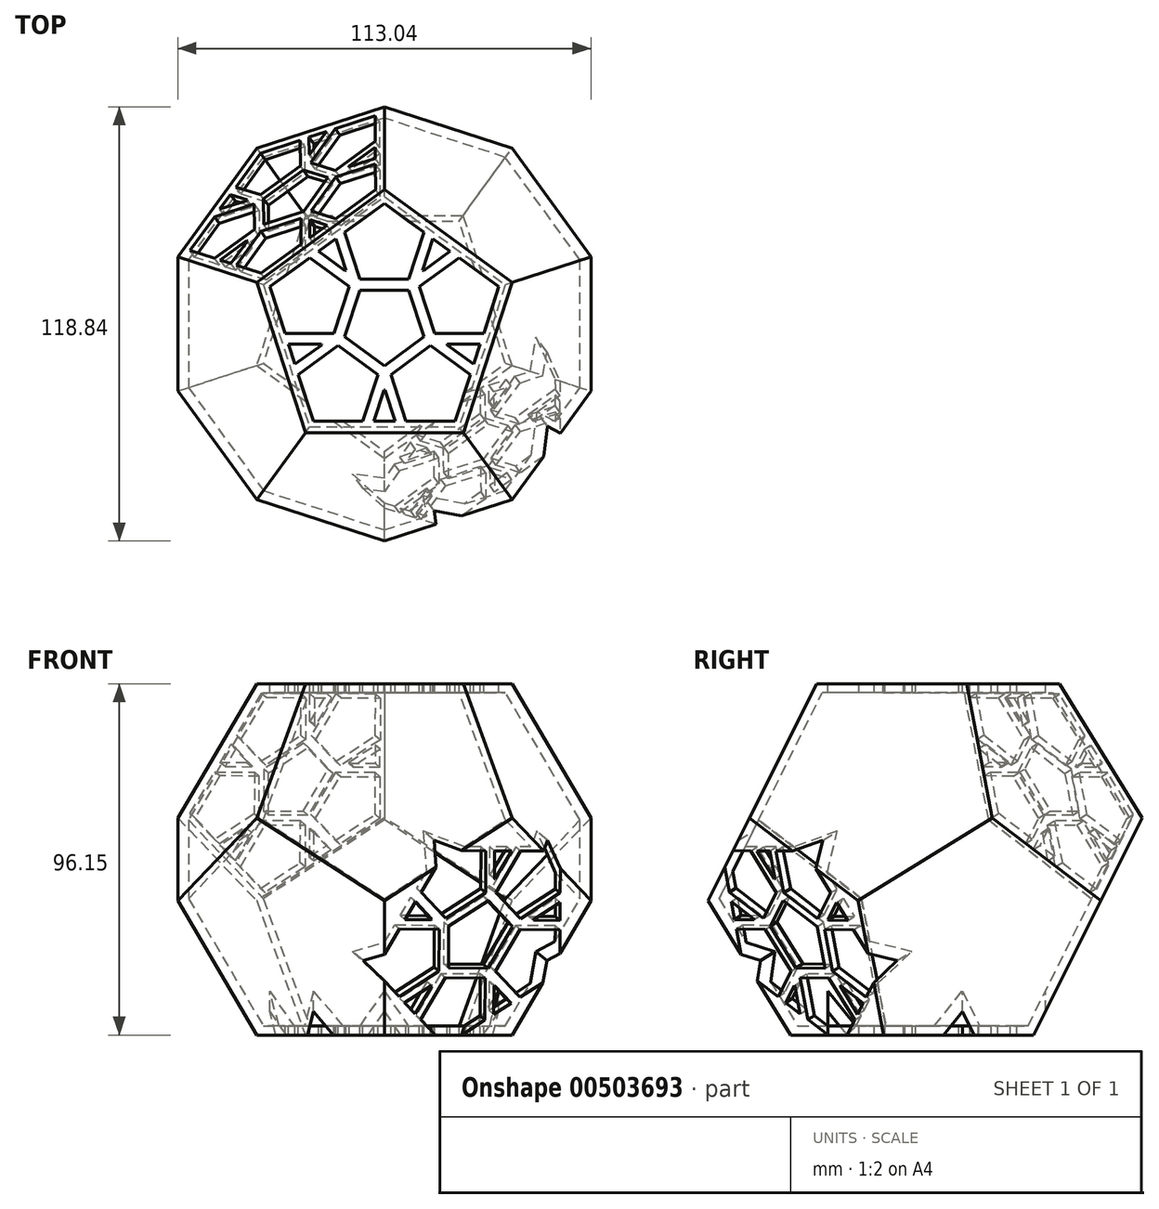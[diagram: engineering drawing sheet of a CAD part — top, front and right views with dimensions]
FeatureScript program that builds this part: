
annotation { "Feature Type Name" : "Feature", "Feature Type Description" : "" }
export const myFeature = defineFeature(function(context is Context, id is Id, definition is map)
    precondition{}
    {
        {
            var Q0;
            Q0=qCreatedBy(makeId("Top.planeOp"),FACE);
            var sketch = newSketch(context, id + "F0", { "sketchPlane" : qUnion([Q0])});
            skCircle(sketch, "E0.cCircle", {"center": v(0, 0) * mm, "radius": 29.71 * mm, "construction": true});
            skLineSegment(sketch, "E0.0", {"start": v(34.93, 11.35) * mm, "end": v(21.59, -29.71) * mm});
            skLineSegment(sketch, "E0.1", {"start": v(21.59, -29.71) * mm, "end": v(-21.59, -29.71) * mm});
            skLineSegment(sketch, "E0.2", {"start": v(-21.59, -29.71) * mm, "end": v(-34.93, 11.35) * mm});
            skLineSegment(sketch, "E0.3", {"start": v(-34.93, 11.35) * mm, "end": v(0, 36.73) * mm});
            skLineSegment(sketch, "E0.4", {"start": v(0, 36.73) * mm, "end": v(34.93, 11.35) * mm});
            skPoint(sketch, "E0.0.midPoint", {"position": v(28.26, -9.18) * mm});
            skLineSegment(sketch, "E1", {"start": v(0, 41.72) * mm, "end": v(0, -38.26) * mm, "construction": true});
            skLineSegment(sketch, "E2", {"start": v(-54.38, 0) * mm, "end": v(61.6, 0) * mm, "construction": true});
            skSolve(sketch);
        }
        {
            var Q0;
            Q0=sQuery(id+"F0.wireOp",EDGE,"E0.2");
            cPlane(context, id + "F1", {"entities" : qUnion([Q0]), "cplaneType" : CPlaneType.LINE_ANGLE, "offset" : 25 * mm, "angle" : 116.57 * degree, "width" : 150 * mm, "height" : 150 * mm});
        }
        {
            var Q0;
            Q0=qCreatedBy(id+"F1.planeOp",FACE);
            var sketch = newSketch(context, id + "F2", { "sketchPlane" : qUnion([Q0])});
            skCircle(sketch, "E3.cCircle", {"center": v(-6.18, -42.55) * mm, "radius": 29.71 * mm, "construction": true});
            skLineSegment(sketch, "E3.0", {"start": v(19.45, -16.25) * mm, "end": v(26.75, -58.8) * mm});
            skLineSegment(sketch, "E3.1", {"start": v(26.75, -58.8) * mm, "end": v(-11.46, -78.9) * mm});
            skLineSegment(sketch, "E3.2", {"start": v(-11.46, -78.9) * mm, "end": v(-42.38, -48.76) * mm});
            skLineSegment(sketch, "E3.3", {"start": v(-42.38, -48.76) * mm, "end": v(-23.27, -10.05) * mm});
            skLineSegment(sketch, "E3.4", {"start": v(-23.27, -10.05) * mm, "end": v(19.45, -16.25) * mm});
            skPoint(sketch, "E3.0.midPoint", {"position": v(23.1, -37.53) * mm});
            skSolve(sketch);
        }
        {
            var Q0;
            Q0=sQuery(id+"F0.wireOp",VERTEX,"E0.1.start");
            var Q1;
            Q1=sQuery(id+"F2.wireOp",VERTEX,"E3.4.start");
            var Q2;
            Q2=sQuery(id+"F2.wireOp",VERTEX,"E3.3.start");
            cPlane(context, id + "F3", {"entities" : qUnion([Q0, Q1, Q2]), "cplaneType" : CPlaneType.THREE_POINT, "offset" : 25 * mm, "oppositeDirection" : true, "width" : 150 * mm, "height" : 150 * mm});
        }
        {
            var Q0;
            Q0=qCreatedBy(id+"F3.planeOp",FACE);
            var sketch = newSketch(context, id + "F4", { "sketchPlane" : qUnion([Q0])});
            skCircle(sketch, "E4.cCircle", {"center": v(0, -43) * mm, "radius": 29.71 * mm, "construction": true});
            skLineSegment(sketch, "E4.0", {"start": v(21.59, -13.29) * mm, "end": v(34.93, -54.35) * mm});
            skLineSegment(sketch, "E4.1", {"start": v(34.93, -54.35) * mm, "end": v(0, -79.73) * mm});
            skLineSegment(sketch, "E4.2", {"start": v(0, -79.73) * mm, "end": v(-34.93, -54.35) * mm});
            skLineSegment(sketch, "E4.3", {"start": v(-34.93, -54.35) * mm, "end": v(-21.59, -13.29) * mm});
            skLineSegment(sketch, "E4.4", {"start": v(-21.59, -13.29) * mm, "end": v(21.59, -13.29) * mm});
            skPoint(sketch, "E4.0.midPoint", {"position": v(28.26, -33.82) * mm});
            skSolve(sketch);
        }
        {
            var Q0;
            Q0=sQuery(id+"F4.wireOp",VERTEX,"E4.2.start");
            var Q1;
            Q1=sQuery(id+"F2.wireOp",VERTEX,"E3.3.start");
            var Q2;
            Q2=sQuery(id+"F2.wireOp",VERTEX,"E3.2.start");
            cPlane(context, id + "F5", {"entities" : qUnion([Q0, Q1, Q2]), "cplaneType" : CPlaneType.THREE_POINT, "offset" : 25 * mm, "width" : 150 * mm, "height" : 150 * mm});
        }
        {
            var Q0;
            Q0=qCreatedBy(id+"F5.planeOp",FACE);
            var sketch = newSketch(context, id + "F6", { "sketchPlane" : qUnion([Q0])});
            skCircle(sketch, "E5.cCircle", {"center": v(-13.29, -40.9) * mm, "radius": 29.71 * mm, "construction": true});
            skLineSegment(sketch, "E5.0", {"start": v(-1.94, -5.97) * mm, "end": v(23.44, -40.9) * mm});
            skLineSegment(sketch, "E5.1", {"start": v(23.44, -40.9) * mm, "end": v(-1.94, -75.82) * mm});
            skLineSegment(sketch, "E5.2", {"start": v(-1.94, -75.82) * mm, "end": v(-43, -62.48) * mm});
            skLineSegment(sketch, "E5.3", {"start": v(-43, -62.48) * mm, "end": v(-43, -19.3) * mm});
            skLineSegment(sketch, "E5.4", {"start": v(-43, -19.3) * mm, "end": v(-1.94, -5.97) * mm});
            skPoint(sketch, "E5.0.midPoint", {"position": v(10.75, -23.43) * mm});
            skSolve(sketch);
        }
        {
            var Q0;
            Q0=sQuery(id+"F4.wireOp",VERTEX,"E4.3.start");
            var Q1;
            Q1=sQuery(id+"F6.wireOp",VERTEX,"E5.3.end");
            var Q2;
            Q2=sQuery(id+"F6.wireOp",VERTEX,"E5.3.start");
            cPlane(context, id + "F7", {"entities" : qUnion([Q0, Q1, Q2]), "cplaneType" : CPlaneType.THREE_POINT, "offset" : 25 * mm, "width" : 150 * mm, "height" : 150 * mm});
        }
        {
            var Q0;
            Q0=qCreatedBy(id+"F7.planeOp",FACE);
            var sketch = newSketch(context, id + "F8", { "sketchPlane" : qUnion([Q0])});
            skCircle(sketch, "E6.cCircle", {"center": v(13.29, -40.9) * mm, "radius": 29.71 * mm, "construction": true});
            skLineSegment(sketch, "E6.0", {"start": v(1.94, -5.97) * mm, "end": v(43, -19.3) * mm});
            skLineSegment(sketch, "E6.1", {"start": v(43, -19.3) * mm, "end": v(43, -62.48) * mm});
            skLineSegment(sketch, "E6.2", {"start": v(43, -62.48) * mm, "end": v(1.94, -75.82) * mm});
            skLineSegment(sketch, "E6.3", {"start": v(1.94, -75.82) * mm, "end": v(-23.44, -40.9) * mm});
            skLineSegment(sketch, "E6.4", {"start": v(-23.44, -40.9) * mm, "end": v(1.94, -5.97) * mm});
            skPoint(sketch, "E6.0.midPoint", {"position": v(22.47, -12.64) * mm});
            skSolve(sketch);
        }
        {
            var Q0;
            Q0=sQuery(id+"F4.wireOp",VERTEX,"E4.4.start");
            var Q1;
            Q1=sQuery(id+"F8.wireOp",VERTEX,"E6.0.start");
            var Q2;
            Q2=sQuery(id+"F8.wireOp",VERTEX,"E6.4.start");
            cPlane(context, id + "F9", {"entities" : qUnion([Q0, Q1, Q2]), "cplaneType" : CPlaneType.THREE_POINT, "offset" : 25 * mm, "width" : 150 * mm, "height" : 150 * mm});
        }
        {
            var Q0;
            Q0=qCreatedBy(id+"F9.planeOp",FACE);
            var sketch = newSketch(context, id + "F10", { "sketchPlane" : qUnion([Q0])});
            skCircle(sketch, "E7.cCircle", {"center": v(6.18, -42.55) * mm, "radius": 29.71 * mm, "construction": true});
            skLineSegment(sketch, "E7.0", {"start": v(-19.45, -16.25) * mm, "end": v(23.27, -10.05) * mm});
            skLineSegment(sketch, "E7.1", {"start": v(23.27, -10.05) * mm, "end": v(42.38, -48.76) * mm});
            skLineSegment(sketch, "E7.2", {"start": v(42.38, -48.76) * mm, "end": v(11.46, -78.9) * mm});
            skLineSegment(sketch, "E7.3", {"start": v(11.46, -78.9) * mm, "end": v(-26.75, -58.8) * mm});
            skLineSegment(sketch, "E7.4", {"start": v(-26.75, -58.8) * mm, "end": v(-19.45, -16.25) * mm});
            skPoint(sketch, "E7.0.midPoint", {"position": v(1.91, -13.15) * mm});
            skSolve(sketch);
        }
        {
            var Q0;
            Q0=sQuery(id+"F0.wireOp",VERTEX,"E0.4.start");
            var Q1;
            Q1=sQuery(id+"F10.wireOp",VERTEX,"E7.0.start");
            var Q2;
            Q2=sQuery(id+"F10.wireOp",VERTEX,"E7.4.start");
            cPlane(context, id + "F11", {"entities" : qUnion([Q0, Q1, Q2]), "cplaneType" : CPlaneType.THREE_POINT, "offset" : 25 * mm, "width" : 150 * mm, "height" : 150 * mm});
        }
        {
            var Q0;
            Q0=qCreatedBy(id+"F11.planeOp",FACE);
            var sketch = newSketch(context, id + "F12", { "sketchPlane" : qUnion([Q0])});
            skCircle(sketch, "E8.cCircle", {"center": v(13.29, -40.9) * mm, "radius": 29.71 * mm, "construction": true});
            skLineSegment(sketch, "E8.0", {"start": v(-16.42, -19.3) * mm, "end": v(24.64, -5.97) * mm});
            skLineSegment(sketch, "E8.1", {"start": v(24.64, -5.97) * mm, "end": v(50.01, -40.9) * mm});
            skLineSegment(sketch, "E8.2", {"start": v(50.01, -40.9) * mm, "end": v(24.64, -75.82) * mm});
            skLineSegment(sketch, "E8.3", {"start": v(24.64, -75.82) * mm, "end": v(-16.42, -62.48) * mm});
            skLineSegment(sketch, "E8.4", {"start": v(-16.42, -62.48) * mm, "end": v(-16.42, -19.3) * mm});
            skPoint(sketch, "E8.0.midPoint", {"position": v(4.1, -12.64) * mm});
            skSolve(sketch);
        }
        {
            var Q0;
            Q0=sQuery(id+"F2.wireOp",VERTEX,"E3.0.start");
            var Q1;
            Q1=sQuery(id+"F12.wireOp",VERTEX,"E8.0.start");
            var Q2;
            Q2=sQuery(id+"F12.wireOp",VERTEX,"E8.4.start");
            cPlane(context, id + "F13", {"entities" : qUnion([Q0, Q1, Q2]), "cplaneType" : CPlaneType.THREE_POINT, "offset" : 25 * mm, "width" : 150 * mm, "height" : 150 * mm});
        }
        {
            var Q0;
            Q0=qCreatedBy(id+"F13.planeOp",FACE);
            var sketch = newSketch(context, id + "F14", { "sketchPlane" : qUnion([Q0])});
            skCircle(sketch, "E9.cCircle", {"center": v(-13.29, -40.9) * mm, "radius": 29.71 * mm, "construction": true});
            skLineSegment(sketch, "E9.0", {"start": v(-50.01, -40.9) * mm, "end": v(-24.64, -5.97) * mm});
            skLineSegment(sketch, "E9.1", {"start": v(-24.64, -5.97) * mm, "end": v(16.42, -19.3) * mm});
            skLineSegment(sketch, "E9.2", {"start": v(16.42, -19.3) * mm, "end": v(16.42, -62.48) * mm});
            skLineSegment(sketch, "E9.3", {"start": v(16.42, -62.48) * mm, "end": v(-24.64, -75.82) * mm});
            skLineSegment(sketch, "E9.4", {"start": v(-24.64, -75.82) * mm, "end": v(-50.01, -40.9) * mm});
            skPoint(sketch, "E9.0.midPoint", {"position": v(-37.33, -23.43) * mm});
            skSolve(sketch);
        }
        {
            var Q0;
            Q0=sQuery(id+"F6.wireOp",VERTEX,"E5.1.start");
            var Q1;
            Q1=sQuery(id+"F14.wireOp",VERTEX,"E9.0.start");
            var Q2;
            Q2=sQuery(id+"F14.wireOp",VERTEX,"E9.4.start");
            cPlane(context, id + "F15", {"entities" : qUnion([Q0, Q1, Q2]), "cplaneType" : CPlaneType.THREE_POINT, "offset" : 25 * mm, "width" : 150 * mm, "height" : 150 * mm});
        }
        {
            var Q0;
            Q0=qCreatedBy(id+"F15.planeOp",FACE);
            var sketch = newSketch(context, id + "F16", { "sketchPlane" : qUnion([Q0])});
            skCircle(sketch, "E10.cCircle", {"center": v(-6.18, -42.55) * mm, "radius": 29.71 * mm, "construction": true});
            skLineSegment(sketch, "E10.0", {"start": v(-39.12, -26.3) * mm, "end": v(-0.9, -6.2) * mm});
            skLineSegment(sketch, "E10.1", {"start": v(-0.9, -6.2) * mm, "end": v(30.01, -36.34) * mm});
            skLineSegment(sketch, "E10.2", {"start": v(30.01, -36.34) * mm, "end": v(10.9, -75.06) * mm});
            skLineSegment(sketch, "E10.3", {"start": v(10.9, -75.06) * mm, "end": v(-31.82, -68.85) * mm});
            skLineSegment(sketch, "E10.4", {"start": v(-31.82, -68.85) * mm, "end": v(-39.12, -26.3) * mm});
            skPoint(sketch, "E10.0.midPoint", {"position": v(-20, -16.25) * mm});
            skSolve(sketch);
        }
        {
            var Q0;
            Q0=sQuery(id+"F12.wireOp",VERTEX,"E8.1.end");
            var Q1;
            Q1=sQuery(id+"F10.wireOp",VERTEX,"E7.3.start");
            var Q2;
            Q2=sQuery(id+"F8.wireOp",VERTEX,"E6.3.start");
            cPlane(context, id + "F17", {"entities" : qUnion([Q0, Q1, Q2]), "cplaneType" : CPlaneType.THREE_POINT, "offset" : 25 * mm, "width" : 150 * mm, "height" : 150 * mm});
        }
        {
            var Q0;
            Q0=qCreatedBy(id+"F17.planeOp",FACE);
            var sketch = newSketch(context, id + "F18", { "sketchPlane" : qUnion([Q0])});
            skCircle(sketch, "E11.cCircle", {"center": v(6.18, -42.55) * mm, "radius": 29.71 * mm, "construction": true});
            skLineSegment(sketch, "E11.0", {"start": v(-30.01, -36.34) * mm, "end": v(0.9, -6.2) * mm});
            skLineSegment(sketch, "E11.1", {"start": v(0.9, -6.2) * mm, "end": v(39.12, -26.3) * mm});
            skLineSegment(sketch, "E11.2", {"start": v(39.12, -26.3) * mm, "end": v(31.82, -68.85) * mm});
            skLineSegment(sketch, "E11.3", {"start": v(31.82, -68.85) * mm, "end": v(-10.9, -75.06) * mm});
            skLineSegment(sketch, "E11.4", {"start": v(-10.9, -75.06) * mm, "end": v(-30.01, -36.34) * mm});
            skPoint(sketch, "E11.0.midPoint", {"position": v(-14.56, -21.28) * mm});
            skSolve(sketch);
        }
        {
            var Q0;
            Q0=sQuery(id+"F18.wireOp",VERTEX,"E11.4.start");
            var Q1;
            Q1=sQuery(id+"F18.wireOp",VERTEX,"E11.3.start");
            var Q2;
            Q2=sQuery(id+"F8.wireOp",VERTEX,"E6.2.start");
            cPlane(context, id + "F19", {"entities" : qUnion([Q0, Q1, Q2]), "cplaneType" : CPlaneType.THREE_POINT, "offset" : 25 * mm, "width" : 150 * mm, "height" : 150 * mm});
        }
        {
            var Q0;
            Q0=qCreatedBy(id+"F19.planeOp",FACE);
            var sketch = newSketch(context, id + "F20", { "sketchPlane" : qUnion([Q0])});
            skCircle(sketch, "E12.cCircle", {"center": v(0, 0) * mm, "radius": 29.71 * mm, "construction": true});
            skLineSegment(sketch, "E12.0", {"start": v(-34.93, -11.35) * mm, "end": v(-21.59, 29.71) * mm});
            skLineSegment(sketch, "E12.1", {"start": v(-21.59, 29.71) * mm, "end": v(21.59, 29.71) * mm});
            skLineSegment(sketch, "E12.2", {"start": v(21.59, 29.71) * mm, "end": v(34.93, -11.35) * mm});
            skLineSegment(sketch, "E12.3", {"start": v(34.93, -11.35) * mm, "end": v(0, -36.73) * mm});
            skLineSegment(sketch, "E12.4", {"start": v(0, -36.73) * mm, "end": v(-34.93, -11.35) * mm});
            skPoint(sketch, "E12.0.midPoint", {"position": v(-28.26, 9.18) * mm});
            skSolve(sketch);
        }
        {
            var Q0;
            Q0=sQuery(id+"F20.wireOp",VERTEX,"E12.2.start");
            var Q1;
            Q1=sQuery(id+"F20.wireOp",VERTEX,"E12.1.start");
            var Q2;
            Q2=sQuery(id+"F14.wireOp",VERTEX,"E9.4.start");
            cPlane(context, id + "F21", {"entities" : qUnion([Q0, Q1, Q2]), "cplaneType" : CPlaneType.THREE_POINT, "offset" : 25 * mm, "width" : 150 * mm, "height" : 150 * mm});
        }
        {
            var Q0;
            Q0=qCreatedBy(id+"F21.planeOp",FACE);
            var sketch = newSketch(context, id + "F22", { "sketchPlane" : qUnion([Q0])});
            skCircle(sketch, "E13.cCircle", {"center": v(0, -43) * mm, "radius": 29.71 * mm, "construction": true});
            skLineSegment(sketch, "E13.0", {"start": v(-34.93, -31.65) * mm, "end": v(0, -6.27) * mm});
            skLineSegment(sketch, "E13.1", {"start": v(0, -6.27) * mm, "end": v(34.93, -31.65) * mm});
            skLineSegment(sketch, "E13.2", {"start": v(34.93, -31.65) * mm, "end": v(21.59, -72.71) * mm});
            skLineSegment(sketch, "E13.3", {"start": v(21.59, -72.71) * mm, "end": v(-21.59, -72.71) * mm});
            skLineSegment(sketch, "E13.4", {"start": v(-21.59, -72.71) * mm, "end": v(-34.93, -31.65) * mm});
            skPoint(sketch, "E13.0.midPoint", {"position": v(-17.46, -18.96) * mm});
            skSolve(sketch);
        }
        {
            var Q0;
            Q0=makeQuery(id+"F2.imprint","IMPRINT",FACE,{"disambiguationData":[TD([[makeQuery(id+"F2.imprint","IMPRINT",EDGE,{"derivedFrom":sQuery(id+"F2.wireOp",EDGE,"E3.0")}),-1.0]])]});
            extrude(context, id + "F23", {"entities" : qUnion([Q0]), "depth" : 2.5 * mm});
        }
        {
            var Q0;
            Q0=makeQuery(id+"F4.imprint","IMPRINT",FACE,{"disambiguationData":[TD([[makeQuery(id+"F4.imprint","IMPRINT",EDGE,{"derivedFrom":sQuery(id+"F4.wireOp",EDGE,"E4.0")}),-1.0]])]});
            extrude(context, id + "F24", {"entities" : qUnion([Q0]), "operationType" : NewBodyOperationType.ADD, "depth" : 2.5 * mm});
        }
        {
            var Q0;
            Q0=makeQuery(id+"F0.imprint","IMPRINT",FACE,{"disambiguationData":[TD([[makeQuery(id+"F0.imprint","IMPRINT",EDGE,{"derivedFrom":sQuery(id+"F0.wireOp",EDGE,"E0.0")}),-1.0]])]});
            extrude(context, id + "F25", {"entities" : qUnion([Q0]), "operationType" : NewBodyOperationType.ADD, "oppositeDirection" : true, "depth" : 2.5 * mm});
        }
        {
            var Q0;
            Q0=makeQuery(id+"F10.imprint","IMPRINT",FACE,{"disambiguationData":[TD([[makeQuery(id+"F10.imprint","IMPRINT",EDGE,{"derivedFrom":sQuery(id+"F10.wireOp",EDGE,"E7.0")}),-1.0]])]});
            extrude(context, id + "F26", {"entities" : qUnion([Q0]), "operationType" : NewBodyOperationType.ADD, "depth" : 2.5 * mm});
        }
        {
            var Q0;
            Q0=makeQuery(id+"F8.imprint","IMPRINT",FACE,{"disambiguationData":[TD([[makeQuery(id+"F8.imprint","IMPRINT",EDGE,{"derivedFrom":sQuery(id+"F8.wireOp",EDGE,"E6.0")}),-1.0]])]});
            extrude(context, id + "F27", {"entities" : qUnion([Q0]), "operationType" : NewBodyOperationType.ADD, "depth" : 2.5 * mm});
        }
        {
            var Q0;
            Q0=makeQuery(id+"F6.imprint","IMPRINT",FACE,{"disambiguationData":[TD([[makeQuery(id+"F6.imprint","IMPRINT",EDGE,{"derivedFrom":sQuery(id+"F6.wireOp",EDGE,"E5.0")}),-1.0]])]});
            extrude(context, id + "F28", {"entities" : qUnion([Q0]), "operationType" : NewBodyOperationType.ADD, "depth" : 2.5 * mm});
        }
        {
            var Q0;
            Q0=makeQuery(id+"F16.imprint","IMPRINT",FACE,{"disambiguationData":[TD([[makeQuery(id+"F16.imprint","IMPRINT",EDGE,{"derivedFrom":sQuery(id+"F16.wireOp",EDGE,"E10.0")}),-1.0]])]});
            extrude(context, id + "F29", {"entities" : qUnion([Q0]), "operationType" : NewBodyOperationType.ADD, "depth" : 2.5 * mm});
        }
        {
            var Q0;
            Q0=makeQuery(id+"F14.imprint","IMPRINT",FACE,{"disambiguationData":[TD([[makeQuery(id+"F14.imprint","IMPRINT",EDGE,{"derivedFrom":sQuery(id+"F14.wireOp",EDGE,"E9.0")}),-1.0]])]});
            extrude(context, id + "F30", {"entities" : qUnion([Q0]), "operationType" : NewBodyOperationType.ADD, "depth" : 2.5 * mm});
        }
        {
            var Q0;
            Q0=makeQuery(id+"F12.imprint","IMPRINT",FACE,{"disambiguationData":[TD([[makeQuery(id+"F12.imprint","IMPRINT",EDGE,{"derivedFrom":sQuery(id+"F12.wireOp",EDGE,"E8.0")}),-1.0]])]});
            extrude(context, id + "F31", {"entities" : qUnion([Q0]), "operationType" : NewBodyOperationType.ADD, "depth" : 2.5 * mm});
        }
        {
            var Q0;
            Q0=makeQuery(id+"F18.imprint","IMPRINT",FACE,{"disambiguationData":[TD([[makeQuery(id+"F18.imprint","IMPRINT",EDGE,{"derivedFrom":sQuery(id+"F18.wireOp",EDGE,"E11.0")}),-1.0]])]});
            extrude(context, id + "F32", {"entities" : qUnion([Q0]), "operationType" : NewBodyOperationType.ADD, "depth" : 2.5 * mm});
        }
        {
            var Q0;
            Q0=makeQuery(id+"F20.imprint","IMPRINT",FACE,{"disambiguationData":[TD([[makeQuery(id+"F20.imprint","IMPRINT",EDGE,{"derivedFrom":sQuery(id+"F20.wireOp",EDGE,"E12.0")}),-1.0]])]});
            extrude(context, id + "F33", {"entities" : qUnion([Q0]), "operationType" : NewBodyOperationType.ADD, "depth" : 2.5 * mm});
        }
        {
            var Q0;
            Q0=makeQuery(id+"F22.imprint","IMPRINT",FACE,{"disambiguationData":[TD([[makeQuery(id+"F22.imprint","IMPRINT",EDGE,{"derivedFrom":sQuery(id+"F22.wireOp",EDGE,"E13.0")}),-1.0]])]});
            extrude(context, id + "F34", {"entities" : qUnion([Q0]), "operationType" : NewBodyOperationType.ADD, "depth" : 2.5 * mm});
        }
        {
            var Q0;
            Q0=makeQuery(id+"F25.opExtrude","CAP_FACE",FACE,{"disambiguationData":[OSD([sQuery(id+"F0.wireOp",EDGE,"E0.0"),sQuery(id+"F0.wireOp",EDGE,"E0.1"),sQuery(id+"F0.wireOp",EDGE,"E0.2"),sQuery(id+"F0.wireOp",EDGE,"E0.3"),sQuery(id+"F0.wireOp",EDGE,"E0.4")])],"isStart":true});
            var sketch = newSketch(context, id + "F35", { "sketchPlane" : qUnion([Q0])});
            skLineSegment(sketch, "E14", {"start": v(-34.93, 11.35) * mm, "end": v(0, 36.73) * mm});
            skLineSegment(sketch, "E15", {"start": v(0, 36.73) * mm, "end": v(34.93, 11.35) * mm});
            skLineSegment(sketch, "E16", {"start": v(34.93, 11.35) * mm, "end": v(21.59, -29.71) * mm});
            skLineSegment(sketch, "E17", {"start": v(21.59, -29.71) * mm, "end": v(-21.59, -29.71) * mm});
            skLineSegment(sketch, "E18", {"start": v(-21.59, -29.71) * mm, "end": v(-34.93, 11.35) * mm});
            skCircle(sketch, "E19.cCircle", {"center": v(-12.64, -17.4) * mm, "radius": 9.25 * mm, "construction": true});
            skLineSegment(sketch, "E19.0", {"start": v(-12.64, -5.96) * mm, "end": v(-1.76, -13.86) * mm});
            skLineSegment(sketch, "E19.1", {"start": v(-1.76, -13.86) * mm, "end": v(-5.92, -26.64) * mm});
            skLineSegment(sketch, "E19.2", {"start": v(-5.92, -26.64) * mm, "end": v(-19.36, -26.64) * mm});
            skLineSegment(sketch, "E19.3", {"start": v(-19.36, -26.64) * mm, "end": v(-23.51, -13.86) * mm});
            skLineSegment(sketch, "E19.4", {"start": v(-23.51, -13.86) * mm, "end": v(-12.64, -5.96) * mm});
            skPoint(sketch, "E19.0.midPoint", {"position": v(-7.2, -9.91) * mm});
            skCircle(sketch, "E20.cCircle", {"center": v(0, 21.5) * mm, "radius": 9.25 * mm, "construction": true});
            skLineSegment(sketch, "E20.0", {"start": v(6.72, 12.25) * mm, "end": v(-6.72, 12.25) * mm});
            skLineSegment(sketch, "E20.1", {"start": v(-6.72, 12.25) * mm, "end": v(-10.87, 25.03) * mm});
            skLineSegment(sketch, "E20.2", {"start": v(-10.87, 25.03) * mm, "end": v(0, 32.93) * mm});
            skLineSegment(sketch, "E20.3", {"start": v(0, 32.93) * mm, "end": v(10.87, 25.03) * mm});
            skLineSegment(sketch, "E20.4", {"start": v(10.87, 25.03) * mm, "end": v(6.72, 12.25) * mm});
            skPoint(sketch, "E20.0.midPoint", {"position": v(0, 12.25) * mm});
            skCircle(sketch, "E21.cCircle", {"center": v(0, 0) * mm, "radius": 9.25 * mm, "construction": true});
            skLineSegment(sketch, "E21.0", {"start": v(-6.72, 9.25) * mm, "end": v(6.72, 9.25) * mm});
            skLineSegment(sketch, "E21.1", {"start": v(6.72, 9.25) * mm, "end": v(10.87, -3.53) * mm});
            skLineSegment(sketch, "E21.2", {"start": v(10.87, -3.53) * mm, "end": v(0, -11.43) * mm});
            skLineSegment(sketch, "E21.3", {"start": v(0, -11.43) * mm, "end": v(-10.87, -3.53) * mm});
            skLineSegment(sketch, "E21.4", {"start": v(-10.87, -3.53) * mm, "end": v(-6.72, 9.25) * mm});
            skPoint(sketch, "E21.0.midPoint", {"position": v(0, 9.25) * mm});
            skPoint(sketch, "E22", {"position": v(28.26, -9.18) * mm});
            skPoint(sketch, "E23", {"position": v(17.46, 24.04) * mm});
            skPoint(sketch, "E24", {"position": v(-17.46, 24.04) * mm});
            skPoint(sketch, "E25", {"position": v(-28.26, -9.18) * mm});
            skPoint(sketch, "E26", {"position": v(0, -29.71) * mm});
            skLineSegment(sketch, "E27", {"start": v(17.46, 24.04) * mm, "end": v(-21.59, -29.71) * mm, "construction": true});
            skLineSegment(sketch, "E28", {"start": v(-17.46, 24.04) * mm, "end": v(21.59, -29.71) * mm});
            skLineSegment(sketch, "E29", {"start": v(28.26, -9.18) * mm, "end": v(-34.93, 11.35) * mm, "construction": true});
            skLineSegment(sketch, "E30", {"start": v(-28.26, -9.18) * mm, "end": v(34.93, 11.35) * mm, "construction": true});
            skCircle(sketch, "E31.cCircle", {"center": v(-20.45, 6.64) * mm, "radius": 9.25 * mm, "construction": true});
            skLineSegment(sketch, "E31.0", {"start": v(-9.57, 10.18) * mm, "end": v(-13.73, -2.6) * mm});
            skLineSegment(sketch, "E31.1", {"start": v(-13.73, -2.6) * mm, "end": v(-27.17, -2.6) * mm});
            skLineSegment(sketch, "E31.2", {"start": v(-27.17, -2.6) * mm, "end": v(-31.32, 10.18) * mm});
            skLineSegment(sketch, "E31.3", {"start": v(-31.32, 10.18) * mm, "end": v(-20.45, 18.08) * mm});
            skLineSegment(sketch, "E31.4", {"start": v(-20.45, 18.08) * mm, "end": v(-9.57, 10.18) * mm});
            skPoint(sketch, "E31.0.midPoint", {"position": v(-11.65, 3.79) * mm});
            skCircle(sketch, "E32.cCircle", {"center": v(20.45, 6.64) * mm, "radius": 9.25 * mm, "construction": true});
            skLineSegment(sketch, "E32.0", {"start": v(9.57, 10.18) * mm, "end": v(13.73, -2.6) * mm});
            skLineSegment(sketch, "E32.1", {"start": v(20.45, 18.08) * mm, "end": v(9.57, 10.18) * mm});
            skLineSegment(sketch, "E32.2", {"start": v(31.32, 10.18) * mm, "end": v(20.45, 18.08) * mm});
            skLineSegment(sketch, "E32.3", {"start": v(27.17, -2.6) * mm, "end": v(31.32, 10.18) * mm});
            skLineSegment(sketch, "E32.4", {"start": v(13.73, -2.6) * mm, "end": v(27.17, -2.6) * mm});
            skPoint(sketch, "E32.0.midPoint", {"position": v(11.65, 3.79) * mm});
            skLineSegment(sketch, "E33", {"start": v(0, 36.73) * mm, "end": v(0, -29.71) * mm, "construction": true});
            skLineSegment(sketch, "E34", {"start": v(-9.57, 10.18) * mm, "end": v(-6.72, 12.25) * mm, "construction": true});
            skLineSegment(sketch, "E35", {"start": v(6.72, 12.25) * mm, "end": v(9.57, 10.18) * mm, "construction": true});
            skLineSegment(sketch, "E36", {"start": v(-12.64, -5.96) * mm, "end": v(-13.73, -2.6) * mm, "construction": true});
            skCircle(sketch, "E37.cCircle", {"center": v(12.64, -17.4) * mm, "radius": 9.25 * mm, "construction": true});
            skLineSegment(sketch, "E37.0", {"start": v(23.51, -13.86) * mm, "end": v(19.36, -26.64) * mm});
            skLineSegment(sketch, "E37.1", {"start": v(19.36, -26.64) * mm, "end": v(5.92, -26.64) * mm});
            skLineSegment(sketch, "E37.2", {"start": v(5.92, -26.64) * mm, "end": v(1.76, -13.86) * mm});
            skLineSegment(sketch, "E37.3", {"start": v(1.76, -13.86) * mm, "end": v(12.64, -5.96) * mm});
            skLineSegment(sketch, "E37.4", {"start": v(12.64, -5.96) * mm, "end": v(23.51, -13.86) * mm});
            skPoint(sketch, "E37.0.midPoint", {"position": v(21.43, -20.25) * mm});
            skPoint(sketch, "E38", {"position": v(7.2, -9.91) * mm});
            skLineSegment(sketch, "E39", {"start": v(12.64, -5.96) * mm, "end": v(13.73, -2.6) * mm, "construction": true});
            skLineSegment(sketch, "E40", {"start": v(-1.76, -13.86) * mm, "end": v(1.76, -13.86) * mm, "construction": true});
            skPoint(sketch, "E41", {"position": v(-8.8, 2.86) * mm});
            skPoint(sketch, "E42", {"position": v(8.8, 2.86) * mm});
            skPoint(sketch, "E43", {"position": v(33.97, 29.48) * mm});
            skPoint(sketch, "E44", {"position": v(-5.44, -7.48) * mm});
            skPoint(sketch, "E45", {"position": v(5.44, -7.48) * mm});
            skLineSegment(sketch, "E46", {"start": v(0, 12.25) * mm, "end": v(0, 9.25) * mm, "construction": true});
            skLineSegment(sketch, "E47", {"start": v(-11.65, 3.79) * mm, "end": v(-8.8, 2.86) * mm, "construction": true});
            skLineSegment(sketch, "E48", {"start": v(11.65, 3.79) * mm, "end": v(8.8, 2.86) * mm, "construction": true});
            skLineSegment(sketch, "E49", {"start": v(5.44, -7.48) * mm, "end": v(7.2, -9.91) * mm, "construction": true});
            skLineSegment(sketch, "E50", {"start": v(-5.44, -7.48) * mm, "end": v(-7.2, -9.91) * mm, "construction": true});
            skLineSegment(sketch, "E51", {"start": v(-18.02, 19.84) * mm, "end": v(-13.3, 23.27) * mm});
            skPoint(sketch, "E52", {"position": v(-15.66, 21.56) * mm});
            skLineSegment(sketch, "E53", {"start": v(-20.45, 18.08) * mm, "end": v(-10.87, 25.03) * mm, "construction": true});
            skLineSegment(sketch, "E54", {"start": v(-10.74, 14.55) * mm, "end": v(-10.52, 14.71) * mm});
            skLineSegment(sketch, "E55", {"start": v(-10.52, 14.71) * mm, "end": v(-13.3, 23.27) * mm});
            skLineSegment(sketch, "E56", {"start": v(-10.74, 14.55) * mm, "end": v(-18.02, 19.84) * mm});
            skLineSegment(sketch, "E57.MirrorCS", {"start": v(10.74, 14.55) * mm, "end": v(18.02, 19.84) * mm});
            skLineSegment(sketch, "E58.MirrorCS", {"start": v(10.52, 14.71) * mm, "end": v(13.3, 23.27) * mm});
            skLineSegment(sketch, "E59.MirrorCS", {"start": v(10.74, 14.55) * mm, "end": v(10.52, 14.71) * mm});
            skLineSegment(sketch, "E60.MirrorCS", {"start": v(20.45, 18.08) * mm, "end": v(10.87, 25.03) * mm, "construction": true});
            skPoint(sketch, "E61.MirrorP", {"position": v(15.66, 21.56) * mm});
            skLineSegment(sketch, "E62.MirrorCS", {"start": v(18.02, 19.84) * mm, "end": v(13.3, 23.27) * mm});
            skLineSegment(sketch, "E63.MirrorCS", {"start": v(-17.24, -5.46) * mm, "end": v(-17.16, -5.72) * mm});
            skLineSegment(sketch, "E64.MirrorCS", {"start": v(-17.24, -5.46) * mm, "end": v(-26.24, -5.46) * mm});
            skLineSegment(sketch, "E65.MirrorCS", {"start": v(-26.24, -5.46) * mm, "end": v(-24.44, -11) * mm});
            skLineSegment(sketch, "E66.MirrorCS", {"start": v(-17.16, -5.72) * mm, "end": v(-24.44, -11) * mm});
            skPoint(sketch, "E67.MirrorP", {"position": v(-25.34, -8.23) * mm});
            skLineSegment(sketch, "E68.MirrorCS", {"start": v(0.14, -18.08) * mm, "end": v(-0.14, -18.08) * mm});
            skLineSegment(sketch, "E69.MirrorCS", {"start": v(0.14, -18.08) * mm, "end": v(2.92, -26.64) * mm});
            skPoint(sketch, "E70.MirrorP", {"position": v(0, -26.64) * mm});
            skLineSegment(sketch, "E71.MirrorCS", {"start": v(2.92, -26.64) * mm, "end": v(-2.92, -26.64) * mm});
            skLineSegment(sketch, "E72.MirrorCS", {"start": v(-0.14, -18.08) * mm, "end": v(-2.92, -26.64) * mm});
            skLineSegment(sketch, "E73.MirrorCS", {"start": v(17.16, -5.72) * mm, "end": v(17.24, -5.46) * mm});
            skLineSegment(sketch, "E74.MirrorCS", {"start": v(17.24, -5.46) * mm, "end": v(26.24, -5.46) * mm});
            skLineSegment(sketch, "E75.MirrorCS", {"start": v(24.44, -11) * mm, "end": v(26.24, -5.46) * mm});
            skLineSegment(sketch, "E76.MirrorCS", {"start": v(17.16, -5.72) * mm, "end": v(24.44, -11) * mm});
            skPoint(sketch, "E77.MirrorP", {"position": v(25.34, -8.23) * mm});
            skSolve(sketch);
        }
        {
            var Q0;
            Q0=makeQuery(id+"F35.imprint","IMPRINT",FACE,{"disambiguationData":[TD([[makeQuery(id+"F35.imprint","IMPRINT",EDGE,{"derivedFrom":sQuery(id+"F35.wireOp",EDGE,"E20.0")}),-1.0]])]});
            var Q1;
            Q1=makeQuery(id+"F35.imprint","IMPRINT",FACE,{"disambiguationData":[TD([[makeQuery(id+"F35.imprint","IMPRINT",EDGE,{"derivedFrom":sQuery(id+"F35.wireOp",EDGE,"E32.0")}),1.0]])]});
            var Q2;
            Q2=makeQuery(id+"F35.imprint","IMPRINT",FACE,{"disambiguationData":[TD([[makeQuery(id+"F35.imprint","IMPRINT",EDGE,{"derivedFrom":sQuery(id+"F35.wireOp",EDGE,"E19.0")}),-1.0]])]});
            var Q3;
            Q3=makeQuery(id+"F35.imprint","IMPRINT",FACE,{"disambiguationData":[TD([[makeQuery(id+"F35.imprint","IMPRINT",EDGE,{"derivedFrom":sQuery(id+"F35.wireOp",EDGE,"E31.0")}),-1.0]])]});
            var Q4;
            {var subQ0=sQuery(id+"F35.wireOp",EDGE,"E21.0");Q4=makeQuery(id+"F35.imprint","IMPRINT",FACE,{"disambiguationData":[TD([[makeQuery(id+"F35.imprint","IMPRINT",EDGE,{"derivedFrom":subQ0}),-1.0]])]});}
            var Q5;
            {var subQ0=sQuery(id+"F35.wireOp",EDGE,"E21.3");Q5=makeQuery(id+"F35.imprint","IMPRINT",FACE,{"disambiguationData":[TD([[makeQuery(id+"F35.imprint","IMPRINT",EDGE,{"derivedFrom":subQ0}),-1.0]])]});}
            var Q6;
            {var subQ0=sQuery(id+"F35.wireOp",EDGE,"E37.1");Q6=makeQuery(id+"F35.imprint","IMPRINT",FACE,{"disambiguationData":[TD([[makeQuery(id+"F35.imprint","IMPRINT",EDGE,{"derivedFrom":subQ0}),-1.0]])]});}
            var Q7;
            {var subQ0=sQuery(id+"F35.wireOp",EDGE,"E37.0");Q7=makeQuery(id+"F35.imprint","IMPRINT",FACE,{"disambiguationData":[TD([[makeQuery(id+"F35.imprint","IMPRINT",EDGE,{"derivedFrom":subQ0}),-1.0]])]});}
            var Q8;
            Q8=makeQuery(id+"F35.imprint","IMPRINT",FACE,{"disambiguationData":[TD([[makeQuery(id+"F35.imprint","IMPRINT",EDGE,{"derivedFrom":sQuery(id+"F35.wireOp",EDGE,"E73.MirrorCS")}),-1.0]])]});
            var Q9;
            Q9=makeQuery(id+"F35.imprint","IMPRINT",FACE,{"disambiguationData":[TD([[makeQuery(id+"F35.imprint","IMPRINT",EDGE,{"derivedFrom":sQuery(id+"F35.wireOp",EDGE,"E57.MirrorCS")}),1.0]])]});
            var Q10;
            Q10=makeQuery(id+"F35.imprint","IMPRINT",FACE,{"disambiguationData":[TD([[makeQuery(id+"F35.imprint","IMPRINT",EDGE,{"derivedFrom":sQuery(id+"F35.wireOp",EDGE,"E68.MirrorCS")}),1.0]])]});
            var Q11;
            Q11=makeQuery(id+"F35.imprint","IMPRINT",FACE,{"disambiguationData":[TD([[makeQuery(id+"F35.imprint","IMPRINT",EDGE,{"derivedFrom":sQuery(id+"F35.wireOp",EDGE,"E63.MirrorCS")}),-1.0]])]});
            var Q12;
            {var subQ5=sQuery(id+"F35.wireOp",EDGE,"E55");Q12=makeQuery(id+"F35.imprint","IMPRINT",FACE,{"disambiguationData":[TD([[makeQuery(id+"F35.imprint","IMPRINT",EDGE,{"derivedFrom":subQ5}),1.0]])]});}
            var Q13;
            {var subQ5=sQuery(id+"F35.wireOp",EDGE,"E56");Q13=makeQuery(id+"F35.imprint","IMPRINT",FACE,{"disambiguationData":[TD([[makeQuery(id+"F35.imprint","IMPRINT",EDGE,{"derivedFrom":subQ5}),-1.0]])]});}
            extrude(context, id + "F36", {"entities" : qUnion([Q0, Q1, Q2, Q3, Q4, Q5, Q6, Q7, Q8, Q9, Q10, Q11, Q12, Q13]), "operationType" : NewBodyOperationType.REMOVE, "endBound" : BoundingType.THROUGH_ALL, "oppositeDirection" : true, "depth" : 25 * mm});
        }
        {
            var Q0;
            Q0=makeQuery(id+"F30.opExtrude","CAP_FACE",FACE,{"disambiguationData":[OSD([sQuery(id+"F14.wireOp",EDGE,"E9.0"),sQuery(id+"F14.wireOp",EDGE,"E9.1"),sQuery(id+"F14.wireOp",EDGE,"E9.2"),sQuery(id+"F14.wireOp",EDGE,"E9.3"),sQuery(id+"F14.wireOp",EDGE,"E9.4")])],"isStart":true});
            var sketch = newSketch(context, id + "F37", { "sketchPlane" : qUnion([Q0])});
            skLineSegment(sketch, "E78", {"start": v(-16.68, -19.5) * mm, "end": v(24.32, -5.97) * mm});
            skLineSegment(sketch, "E79", {"start": v(24.32, -5.97) * mm, "end": v(49.86, -40.78) * mm});
            skLineSegment(sketch, "E80", {"start": v(49.86, -40.78) * mm, "end": v(24.64, -75.82) * mm});
            skLineSegment(sketch, "E81", {"start": v(24.64, -75.82) * mm, "end": v(-16.48, -62.67) * mm});
            skLineSegment(sketch, "E82", {"start": v(-16.48, -62.67) * mm, "end": v(-16.68, -19.5) * mm});
            skCircle(sketch, "E83.cCircle", {"center": v(-4.2, -53.66) * mm, "radius": 9.25 * mm, "construction": true});
            skLineSegment(sketch, "E83.0", {"start": v(-0.72, -42.77) * mm, "end": v(7.23, -53.61) * mm});
            skLineSegment(sketch, "E83.1", {"start": v(7.23, -53.61) * mm, "end": v(-0.62, -64.52) * mm});
            skLineSegment(sketch, "E83.2", {"start": v(-0.62, -64.52) * mm, "end": v(-13.43, -60.42) * mm});
            skLineSegment(sketch, "E83.3", {"start": v(-13.43, -60.42) * mm, "end": v(-13.49, -46.98) * mm});
            skLineSegment(sketch, "E83.4", {"start": v(-13.49, -46.98) * mm, "end": v(-0.72, -42.77) * mm});
            skPoint(sketch, "E83.0.midPoint", {"position": v(3.25, -48.2) * mm});
            skCircle(sketch, "E84.cCircle", {"center": v(19.68, -20.47) * mm, "radius": 9.25 * mm, "construction": true});
            skLineSegment(sketch, "E84.0", {"start": v(23.27, -31.33) * mm, "end": v(10.46, -27.23) * mm});
            skLineSegment(sketch, "E84.1", {"start": v(10.46, -27.23) * mm, "end": v(10.4, -13.8) * mm});
            skLineSegment(sketch, "E84.2", {"start": v(10.4, -13.8) * mm, "end": v(23.17, -9.58) * mm});
            skLineSegment(sketch, "E84.3", {"start": v(23.17, -9.58) * mm, "end": v(31.12, -20.42) * mm});
            skLineSegment(sketch, "E84.4", {"start": v(31.12, -20.42) * mm, "end": v(23.27, -31.33) * mm});
            skPoint(sketch, "E84.0.midPoint", {"position": v(16.86, -29.28) * mm});
            skCircle(sketch, "E85.cCircle", {"center": v(13.13, -40.95) * mm, "radius": 9.25 * mm, "construction": true});
            skLineSegment(sketch, "E85.0", {"start": v(9.55, -30.09) * mm, "end": v(22.35, -34.18) * mm});
            skLineSegment(sketch, "E85.1", {"start": v(22.35, -34.18) * mm, "end": v(22.41, -47.63) * mm});
            skLineSegment(sketch, "E85.2", {"start": v(22.41, -47.63) * mm, "end": v(9.65, -51.84) * mm});
            skLineSegment(sketch, "E85.3", {"start": v(9.65, -51.84) * mm, "end": v(1.7, -41) * mm});
            skLineSegment(sketch, "E85.4", {"start": v(1.7, -41) * mm, "end": v(9.55, -30.09) * mm});
            skPoint(sketch, "E85.0.midPoint", {"position": v(15.95, -32.14) * mm});
            skPoint(sketch, "E86", {"position": v(37.25, -58.3) * mm});
            skPoint(sketch, "E87", {"position": v(37.1, -23.37) * mm});
            skPoint(sketch, "E88", {"position": v(3.82, -12.73) * mm});
            skPoint(sketch, "E89", {"position": v(-16.58, -41.08) * mm});
            skPoint(sketch, "E90", {"position": v(4.08, -69.25) * mm});
            skLineSegment(sketch, "E91", {"start": v(37.1, -23.37) * mm, "end": v(-16.48, -62.67) * mm, "construction": true});
            skLineSegment(sketch, "E92", {"start": v(3.82, -12.73) * mm, "end": v(24.64, -75.82) * mm, "construction": true});
            skLineSegment(sketch, "E93", {"start": v(37.25, -58.3) * mm, "end": v(-16.68, -19.5) * mm, "construction": true});
            skLineSegment(sketch, "E94", {"start": v(-16.58, -41.08) * mm, "end": v(49.86, -40.78) * mm, "construction": true});
            skCircle(sketch, "E95.cCircle", {"center": v(-4.32, -28.39) * mm, "radius": 9.25 * mm, "construction": true});
            skLineSegment(sketch, "E95.0", {"start": v(7.11, -28.34) * mm, "end": v(-0.74, -39.25) * mm});
            skLineSegment(sketch, "E95.1", {"start": v(-0.74, -39.25) * mm, "end": v(-13.54, -35.15) * mm});
            skLineSegment(sketch, "E95.2", {"start": v(-13.54, -35.15) * mm, "end": v(-13.6, -21.7) * mm});
            skLineSegment(sketch, "E95.3", {"start": v(-13.6, -21.7) * mm, "end": v(-0.83, -17.5) * mm});
            skLineSegment(sketch, "E95.4", {"start": v(-0.83, -17.5) * mm, "end": v(7.11, -28.34) * mm});
            skPoint(sketch, "E95.0.midPoint", {"position": v(3.19, -33.8) * mm});
            skCircle(sketch, "E96.cCircle", {"center": v(34.63, -40.85) * mm, "radius": 9.25 * mm, "construction": true});
            skLineSegment(sketch, "E96.0", {"start": v(25.35, -34.17) * mm, "end": v(25.41, -47.61) * mm});
            skLineSegment(sketch, "E96.1", {"start": v(38.12, -29.96) * mm, "end": v(25.35, -34.17) * mm});
            skLineSegment(sketch, "E96.2", {"start": v(46.06, -40.8) * mm, "end": v(38.12, -29.96) * mm});
            skLineSegment(sketch, "E96.3", {"start": v(38.21, -51.7) * mm, "end": v(46.06, -40.8) * mm});
            skLineSegment(sketch, "E96.4", {"start": v(25.41, -47.61) * mm, "end": v(38.21, -51.7) * mm});
            skPoint(sketch, "E96.0.midPoint", {"position": v(25.38, -40.9) * mm});
            skLineSegment(sketch, "E97", {"start": v(24.32, -5.97) * mm, "end": v(4.08, -69.25) * mm, "construction": true});
            skLineSegment(sketch, "E98", {"start": v(7.11, -28.34) * mm, "end": v(10.46, -27.23) * mm, "construction": true});
            skLineSegment(sketch, "E99", {"start": v(23.27, -31.33) * mm, "end": v(25.35, -34.17) * mm, "construction": true});
            skLineSegment(sketch, "E100", {"start": v(-0.72, -42.77) * mm, "end": v(-0.74, -39.25) * mm, "construction": true});
            skCircle(sketch, "E101.cCircle", {"center": v(19.87, -61.36) * mm, "radius": 9.25 * mm, "construction": true});
            skLineSegment(sketch, "E101.0", {"start": v(31.3, -61.31) * mm, "end": v(23.45, -72.22) * mm});
            skLineSegment(sketch, "E101.1", {"start": v(23.45, -72.22) * mm, "end": v(10.65, -68.13) * mm});
            skLineSegment(sketch, "E101.2", {"start": v(10.65, -68.13) * mm, "end": v(10.59, -54.69) * mm});
            skLineSegment(sketch, "E101.3", {"start": v(10.59, -54.69) * mm, "end": v(23.35, -50.47) * mm});
            skLineSegment(sketch, "E101.4", {"start": v(23.35, -50.47) * mm, "end": v(31.3, -61.31) * mm});
            skPoint(sketch, "E101.0.midPoint", {"position": v(27.37, -66.77) * mm});
            skPoint(sketch, "E102", {"position": v(16.97, -52.58) * mm});
            skLineSegment(sketch, "E103", {"start": v(23.35, -50.47) * mm, "end": v(25.41, -47.61) * mm, "construction": true});
            skLineSegment(sketch, "E104", {"start": v(7.23, -53.61) * mm, "end": v(10.59, -54.69) * mm, "construction": true});
            skPoint(sketch, "E105", {"position": v(5.62, -35.54) * mm});
            skPoint(sketch, "E106", {"position": v(22.38, -40.9) * mm});
            skPoint(sketch, "E107", {"position": v(33.66, 29.4) * mm});
            skPoint(sketch, "E108", {"position": v(5.67, -46.42) * mm});
            skPoint(sketch, "E109", {"position": v(16.03, -49.73) * mm});
            skLineSegment(sketch, "E110", {"start": v(16.86, -29.28) * mm, "end": v(15.95, -32.14) * mm, "construction": true});
            skLineSegment(sketch, "E111", {"start": v(3.19, -33.8) * mm, "end": v(5.62, -35.54) * mm, "construction": true});
            skLineSegment(sketch, "E112", {"start": v(25.38, -40.9) * mm, "end": v(22.38, -40.9) * mm, "construction": true});
            skLineSegment(sketch, "E113", {"start": v(16.03, -49.73) * mm, "end": v(16.97, -52.58) * mm, "construction": true});
            skLineSegment(sketch, "E114", {"start": v(5.67, -46.42) * mm, "end": v(3.25, -48.2) * mm, "construction": true});
            skLineSegment(sketch, "E115", {"start": v(2.01, -16.56) * mm, "end": v(7.55, -14.73) * mm});
            skPoint(sketch, "E116", {"position": v(4.78, -15.64) * mm});
            skLineSegment(sketch, "E117", {"start": v(-0.83, -17.5) * mm, "end": v(10.4, -13.8) * mm, "construction": true});
            skLineSegment(sketch, "E118", {"start": v(7.34, -23.81) * mm, "end": v(7.6, -23.73) * mm});
            skLineSegment(sketch, "E119", {"start": v(7.6, -23.73) * mm, "end": v(7.55, -14.73) * mm});
            skLineSegment(sketch, "E120", {"start": v(7.34, -23.81) * mm, "end": v(2.01, -16.56) * mm});
            skLineSegment(sketch, "E121.MirrorCS", {"start": v(27.8, -30.36) * mm, "end": v(36.34, -27.54) * mm});
            skLineSegment(sketch, "E122.MirrorCS", {"start": v(27.63, -30.14) * mm, "end": v(32.9, -22.84) * mm});
            skLineSegment(sketch, "E123.MirrorCS", {"start": v(27.8, -30.36) * mm, "end": v(27.63, -30.14) * mm});
            skLineSegment(sketch, "E124.MirrorCS", {"start": v(38.12, -29.96) * mm, "end": v(31.12, -20.42) * mm, "construction": true});
            skPoint(sketch, "E125.MirrorP", {"position": v(34.62, -25.19) * mm});
            skLineSegment(sketch, "E126.MirrorCS", {"start": v(36.34, -27.54) * mm, "end": v(32.9, -22.84) * mm});
            skLineSegment(sketch, "E127.MirrorCS", {"start": v(-4.95, -40.9) * mm, "end": v(-4.95, -41.16) * mm});
            skLineSegment(sketch, "E128.MirrorCS", {"start": v(-4.95, -40.9) * mm, "end": v(-13.53, -38.15) * mm});
            skLineSegment(sketch, "E129.MirrorCS", {"start": v(-13.53, -38.15) * mm, "end": v(-13.5, -43.98) * mm});
            skLineSegment(sketch, "E130.MirrorCS", {"start": v(-4.95, -41.16) * mm, "end": v(-13.5, -43.98) * mm});
            skPoint(sketch, "E131.MirrorP", {"position": v(-13.51, -41.07) * mm});
            skLineSegment(sketch, "E132.MirrorCS", {"start": v(7.75, -58.21) * mm, "end": v(7.5, -58.13) * mm});
            skLineSegment(sketch, "E133.MirrorCS", {"start": v(7.75, -58.21) * mm, "end": v(7.79, -67.21) * mm});
            skPoint(sketch, "E134.MirrorP", {"position": v(5.01, -66.32) * mm});
            skLineSegment(sketch, "E135.MirrorCS", {"start": v(7.79, -67.21) * mm, "end": v(2.23, -65.43) * mm});
            skLineSegment(sketch, "E136.MirrorCS", {"start": v(7.5, -58.13) * mm, "end": v(2.23, -65.43) * mm});
            skLineSegment(sketch, "E137.MirrorCS", {"start": v(27.73, -51.62) * mm, "end": v(27.89, -51.4) * mm});
            skLineSegment(sketch, "E138.MirrorCS", {"start": v(27.89, -51.4) * mm, "end": v(36.46, -54.14) * mm});
            skLineSegment(sketch, "E139.MirrorCS", {"start": v(33.05, -58.88) * mm, "end": v(36.46, -54.14) * mm});
            skLineSegment(sketch, "E140.MirrorCS", {"start": v(27.73, -51.62) * mm, "end": v(33.05, -58.88) * mm});
            skPoint(sketch, "E141.MirrorP", {"position": v(34.76, -56.51) * mm});
            skSolve(sketch);
        }
        {
            var Q0;
            Q0=makeQuery(id+"F37.imprint","IMPRINT",FACE,{"disambiguationData":[TD([[makeQuery(id+"F37.imprint","IMPRINT",EDGE,{"derivedFrom":sQuery(id+"F37.wireOp",EDGE,"E101.0")}),-1.0]])]});
            var Q1;
            Q1=makeQuery(id+"F37.imprint","IMPRINT",FACE,{"disambiguationData":[TD([[makeQuery(id+"F37.imprint","IMPRINT",EDGE,{"derivedFrom":sQuery(id+"F37.wireOp",EDGE,"E96.0")}),1.0]])]});
            var Q2;
            Q2=makeQuery(id+"F37.imprint","IMPRINT",FACE,{"disambiguationData":[TD([[makeQuery(id+"F37.imprint","IMPRINT",EDGE,{"derivedFrom":sQuery(id+"F37.wireOp",EDGE,"E84.0")}),-1.0]])]});
            var Q3;
            Q3=makeQuery(id+"F37.imprint","IMPRINT",FACE,{"disambiguationData":[TD([[makeQuery(id+"F37.imprint","IMPRINT",EDGE,{"derivedFrom":sQuery(id+"F37.wireOp",EDGE,"E95.0")}),-1.0]])]});
            var Q4;
            Q4=makeQuery(id+"F37.imprint","IMPRINT",FACE,{"disambiguationData":[TD([[makeQuery(id+"F37.imprint","IMPRINT",EDGE,{"derivedFrom":sQuery(id+"F37.wireOp",EDGE,"E83.0")}),-1.0]])]});
            var Q5;
            Q5=makeQuery(id+"F37.imprint","IMPRINT",FACE,{"disambiguationData":[TD([[makeQuery(id+"F37.imprint","IMPRINT",EDGE,{"derivedFrom":sQuery(id+"F37.wireOp",EDGE,"E85.0")}),-1.0]])]});
            var Q6;
            Q6=makeQuery(id+"F37.imprint","IMPRINT",FACE,{"disambiguationData":[TD([[makeQuery(id+"F37.imprint","IMPRINT",EDGE,{"derivedFrom":sQuery(id+"F37.wireOp",EDGE,"E115")}),-1.0]])]});
            var Q7;
            Q7=makeQuery(id+"F37.imprint","IMPRINT",FACE,{"disambiguationData":[TD([[makeQuery(id+"F37.imprint","IMPRINT",EDGE,{"derivedFrom":sQuery(id+"F37.wireOp",EDGE,"E127.MirrorCS")}),-1.0]])]});
            var Q8;
            Q8=makeQuery(id+"F37.imprint","IMPRINT",FACE,{"disambiguationData":[TD([[makeQuery(id+"F37.imprint","IMPRINT",EDGE,{"derivedFrom":sQuery(id+"F37.wireOp",EDGE,"E132.MirrorCS")}),1.0]])]});
            var Q9;
            Q9=makeQuery(id+"F37.imprint","IMPRINT",FACE,{"disambiguationData":[TD([[makeQuery(id+"F37.imprint","IMPRINT",EDGE,{"derivedFrom":sQuery(id+"F37.wireOp",EDGE,"E137.MirrorCS")}),-1.0]])]});
            var Q10;
            Q10=makeQuery(id+"F37.imprint","IMPRINT",FACE,{"disambiguationData":[TD([[makeQuery(id+"F37.imprint","IMPRINT",EDGE,{"derivedFrom":sQuery(id+"F37.wireOp",EDGE,"E121.MirrorCS")}),1.0]])]});
            extrude(context, id + "F38", {"entities" : qUnion([Q0, Q1, Q2, Q3, Q4, Q5, Q6, Q7, Q8, Q9, Q10]), "operationType" : NewBodyOperationType.REMOVE, "endBound" : BoundingType.THROUGH_ALL, "oppositeDirection" : true, "depth" : 25 * mm});
        }
    });
